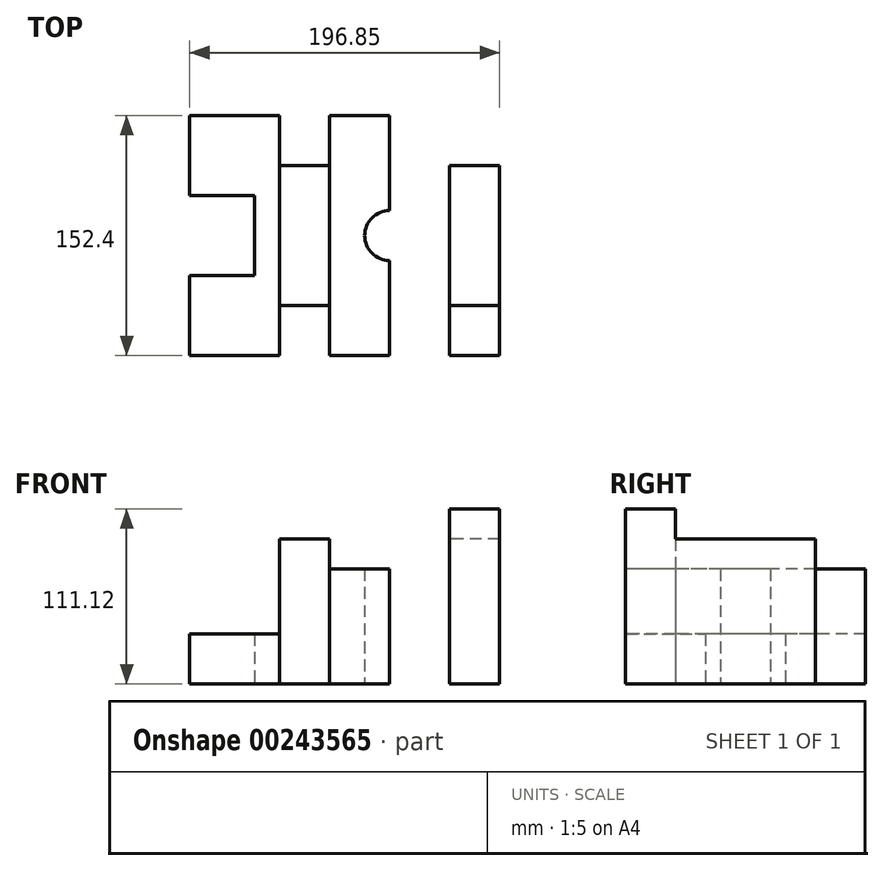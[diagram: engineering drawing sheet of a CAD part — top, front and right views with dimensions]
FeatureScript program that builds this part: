
annotation { "Feature Type Name" : "Feature", "Feature Type Description" : "" }
export const myFeature = defineFeature(function(context is Context, id is Id, definition is map)
    precondition{}
    {
        {
            var Q0;
            Q0=qCreatedBy(makeId("Top.planeOp"),FACE);
            var sketch = newSketch(context, id + "F0", { "sketchPlane" : qUnion([Q0])});
            skLineSegment(sketch, "E0.bottom", {"start": v(127, 76.2) * mm, "end": v(-127, 76.2) * mm});
            skLineSegment(sketch, "E0.top", {"start": v(127, -76.2) * mm, "end": v(-127, -76.2) * mm});
            skLineSegment(sketch, "E0.left", {"start": v(127, 76.2) * mm, "end": v(127, 25.4) * mm});
            skLineSegment(sketch, "E0.right", {"start": v(-127, 76.2) * mm, "end": v(-127, 25.4) * mm});
            skPoint(sketch, "E0.middle", {"position": v(0, 0) * mm});
            skCircle(sketch, "E1", {"center": v(0, 0) * mm, "radius": 15.88 * mm});
            skLineSegment(sketch, "E2.bottom", {"start": v(69.85, 76.2) * mm, "end": v(-69.85, 76.2) * mm});
            skLineSegment(sketch, "E2.top", {"start": v(69.85, -76.2) * mm, "end": v(-69.85, -76.2) * mm});
            skLineSegment(sketch, "E2.left", {"start": v(69.85, 76.2) * mm, "end": v(69.85, -76.2) * mm});
            skLineSegment(sketch, "E2.right", {"start": v(-69.85, 76.2) * mm, "end": v(-69.85, -76.2) * mm});
            skLineSegment(sketch, "E3.bottom", {"start": v(-69.85, 76.2) * mm, "end": v(-38.1, 76.2) * mm});
            skLineSegment(sketch, "E3.top", {"start": v(-69.85, -76.2) * mm, "end": v(-38.1, -76.2) * mm});
            skLineSegment(sketch, "E3.right", {"start": v(-38.1, 76.2) * mm, "end": v(-38.1, -76.2) * mm});
            skLineSegment(sketch, "E4", {"start": v(0, 76.2) * mm, "end": v(0, -76.2) * mm});
            skLineSegment(sketch, "E5.top", {"start": v(-69.85, 44.45) * mm, "end": v(-38.1, 44.45) * mm});
            skLineSegment(sketch, "E5.left", {"start": v(-69.85, 76.2) * mm, "end": v(-69.85, 44.45) * mm});
            skLineSegment(sketch, "E5.right", {"start": v(-38.1, 76.2) * mm, "end": v(-38.1, 44.45) * mm});
            skLineSegment(sketch, "E6.top", {"start": v(-69.85, -44.45) * mm, "end": v(-38.1, -44.45) * mm});
            skLineSegment(sketch, "E6.left", {"start": v(-69.85, -76.2) * mm, "end": v(-69.85, -44.45) * mm});
            skLineSegment(sketch, "E6.right", {"start": v(-38.1, -76.2) * mm, "end": v(-38.1, -44.45) * mm});
            skLineSegment(sketch, "E7.bottom", {"start": v(-127, 76.2) * mm, "end": v(-69.85, 76.2) * mm});
            skLineSegment(sketch, "E7.top", {"start": v(-127, 25.4) * mm, "end": v(-85.72, 25.4) * mm});
            skLineSegment(sketch, "E7.right", {"start": v(-69.85, 76.2) * mm, "end": v(-69.85, 25.4) * mm});
            skLineSegment(sketch, "E8.bottom", {"start": v(-127, -76.2) * mm, "end": v(-69.85, -76.2) * mm});
            skLineSegment(sketch, "E8.top", {"start": v(-127, -25.4) * mm, "end": v(-85.72, -25.4) * mm});
            skLineSegment(sketch, "E8.left", {"start": v(-127, -76.2) * mm, "end": v(-127, -25.4) * mm});
            skLineSegment(sketch, "E8.right", {"start": v(-69.85, -76.2) * mm, "end": v(-69.85, -25.4) * mm});
            skLineSegment(sketch, "E9.right", {"start": v(-85.72, 25.4) * mm, "end": v(-85.72, -25.4) * mm});
            skLineSegment(sketch, "E10.trimOffspring", {"start": v(-127, -25.4) * mm, "end": v(-127, -76.2) * mm});
            skLineSegment(sketch, "E11.MirrorCS", {"start": v(69.85, -76.2) * mm, "end": v(38.1, -76.2) * mm});
            skLineSegment(sketch, "E12.MirrorCS", {"start": v(127, -25.4) * mm, "end": v(85.72, -25.4) * mm});
            skLineSegment(sketch, "E13.MirrorCS", {"start": v(127, 25.4) * mm, "end": v(85.72, 25.4) * mm});
            skLineSegment(sketch, "E14.MirrorCS", {"start": v(69.85, -76.2) * mm, "end": v(69.85, -44.45) * mm});
            skLineSegment(sketch, "E15.MirrorCS", {"start": v(69.85, 76.2) * mm, "end": v(69.85, 44.45) * mm});
            skLineSegment(sketch, "E16.MirrorCS", {"start": v(127, -76.2) * mm, "end": v(127, -25.4) * mm});
            skLineSegment(sketch, "E17.MirrorCS", {"start": v(69.85, 76.2) * mm, "end": v(38.1, 76.2) * mm});
            skLineSegment(sketch, "E18.MirrorCS", {"start": v(127, 76.2) * mm, "end": v(69.85, 76.2) * mm});
            skLineSegment(sketch, "E19.MirrorCS", {"start": v(69.85, 76.2) * mm, "end": v(69.85, 25.4) * mm});
            skLineSegment(sketch, "E20.MirrorCS", {"start": v(127, -76.2) * mm, "end": v(69.85, -76.2) * mm});
            skLineSegment(sketch, "E21.MirrorCS", {"start": v(69.85, -44.45) * mm, "end": v(38.1, -44.45) * mm});
            skLineSegment(sketch, "E22.MirrorCS", {"start": v(85.72, 25.4) * mm, "end": v(85.72, -25.4) * mm});
            skLineSegment(sketch, "E23.MirrorCS", {"start": v(38.1, -76.2) * mm, "end": v(38.1, -44.45) * mm});
            skLineSegment(sketch, "E24.MirrorCS", {"start": v(127, -25.4) * mm, "end": v(127, -76.2) * mm});
            skLineSegment(sketch, "E25.MirrorCS", {"start": v(69.85, -76.2) * mm, "end": v(69.85, -25.4) * mm});
            skLineSegment(sketch, "E26.MirrorCS", {"start": v(38.1, 76.2) * mm, "end": v(38.1, -76.2) * mm});
            skLineSegment(sketch, "E27.MirrorCS", {"start": v(38.1, 76.2) * mm, "end": v(38.1, 44.45) * mm});
            skLineSegment(sketch, "E28.MirrorCS", {"start": v(69.85, 44.45) * mm, "end": v(38.1, 44.45) * mm});
            skSolve(sketch);
        }
        {
            var Q0;
            {var subQ1=sQuery(id+"F0.wireOp",EDGE,"E2.right");Q0=makeQuery(id+"F0.imprint","IMPRINT",FACE,{"disambiguationData":[TD([[makeQuery(id+"F0.imprint","IMPRINT",EDGE,{"derivedFrom":subQ1}),-1.0]])]});}
            var Q1;
            {var subQ7=sQuery(id+"F0.wireOp",EDGE,"E18.MirrorCS");Q1=makeQuery(id+"F0.imprint","IMPRINT",FACE,{"disambiguationData":[TD([[makeQuery(id+"F0.imprint","IMPRINT",EDGE,{"derivedFrom":subQ7}),1.0]])]});}
            var Q2;
            {var subQ2=sQuery(id+"F0.wireOp",EDGE,"E2.right");Q2=makeQuery(id+"F0.imprint","IMPRINT",FACE,{"disambiguationData":[TD([[makeQuery(id+"F0.imprint","IMPRINT",EDGE,{"derivedFrom":subQ2}),1.0]])]});}
            var Q3;
            {var subQ0=sQuery(id+"F0.wireOp",EDGE,"E3.bottom");Q3=makeQuery(id+"F0.imprint","IMPRINT",FACE,{"disambiguationData":[TD([[makeQuery(id+"F0.imprint","IMPRINT",EDGE,{"derivedFrom":subQ0}),-1.0]])]});}
            var Q4;
            {var subQ0=sQuery(id+"F0.wireOp",EDGE,"E3.top");Q4=makeQuery(id+"F0.imprint","IMPRINT",FACE,{"disambiguationData":[TD([[makeQuery(id+"F0.imprint","IMPRINT",EDGE,{"derivedFrom":subQ0}),1.0]])]});}
            var Q5;
            Q5=makeQuery(id+"F0.imprint","IMPRINT",FACE,{"disambiguationData":[TD([[makeQuery(id+"F0.imprint","IMPRINT",EDGE,{"derivedFrom":sQuery(id+"F0.wireOp",EDGE,"E3.right")}),1.0]])]});
            var Q6;
            {var subQ11=sQuery(id+"F0.wireOp",EDGE,"E27.MirrorCS");Q6=makeQuery(id+"F0.imprint","IMPRINT",FACE,{"disambiguationData":[TD([[makeQuery(id+"F0.imprint","IMPRINT",EDGE,{"derivedFrom":subQ11}),-1.0]])]});}
            var Q7;
            {var subQ0=sQuery(id+"F0.wireOp",EDGE,"E21.MirrorCS");Q7=makeQuery(id+"F0.imprint","IMPRINT",FACE,{"disambiguationData":[TD([[makeQuery(id+"F0.imprint","IMPRINT",EDGE,{"derivedFrom":subQ0}),1.0]])]});}
            var Q8;
            {var subQ1=sQuery(id+"F0.wireOp",EDGE,"E21.MirrorCS");Q8=makeQuery(id+"F0.imprint","IMPRINT",FACE,{"disambiguationData":[TD([[makeQuery(id+"F0.imprint","IMPRINT",EDGE,{"derivedFrom":subQ1}),-1.0]])]});}
            var Q9;
            {var subQ0=sQuery(id+"F0.wireOp",EDGE,"E17.MirrorCS");Q9=makeQuery(id+"F0.imprint","IMPRINT",FACE,{"disambiguationData":[TD([[makeQuery(id+"F0.imprint","IMPRINT",EDGE,{"derivedFrom":subQ0}),1.0]])]});}
            extrude(context, id + "F1", {"entities" : qUnion([Q0, Q1, Q2, Q3, Q4, Q5, Q6, Q7, Q8, Q9]), "depth" : 31.75 * mm});
        }
        {
            var Q0;
            Q0=makeQuery(id+"F1.opExtrude","CAP_FACE",FACE,{"disambiguationData":[OSD([sQuery(id+"F0.wireOp",EDGE,"E1"),sQuery(id+"F0.wireOp",EDGE,"E2.bottom"),sQuery(id+"F0.wireOp",EDGE,"E2.top"),sQuery(id+"F0.wireOp",EDGE,"E3.bottom"),sQuery(id+"F0.wireOp",EDGE,"E3.top"),sQuery(id+"F0.wireOp",EDGE,"E7.bottom"),sQuery(id+"F0.wireOp",EDGE,"E0.right"),sQuery(id+"F0.wireOp",EDGE,"E8.bottom"),sQuery(id+"F0.wireOp",EDGE,"E7.top"),sQuery(id+"F0.wireOp",EDGE,"E8.top"),sQuery(id+"F0.wireOp",EDGE,"E9.right"),sQuery(id+"F0.wireOp",EDGE,"E10.trimOffspring"),sQuery(id+"F0.wireOp",EDGE,"E18.MirrorCS"),sQuery(id+"F0.wireOp",EDGE,"E12.MirrorCS"),sQuery(id+"F0.wireOp",EDGE,"E20.MirrorCS"),sQuery(id+"F0.wireOp",EDGE,"E22.MirrorCS"),sQuery(id+"F0.wireOp",EDGE,"E17.MirrorCS"),sQuery(id+"F0.wireOp",EDGE,"E11.MirrorCS"),sQuery(id+"F0.wireOp",EDGE,"E13.MirrorCS"),sQuery(id+"F0.wireOp",EDGE,"E0.left"),sQuery(id+"F0.wireOp",EDGE,"E24.MirrorCS")])],"isStart":false});
            var sketch = newSketch(context, id + "F2", { "sketchPlane" : qUnion([Q0])});
            skLineSegment(sketch, "E29.bottom", {"start": v(127, 76.2) * mm, "end": v(-127, 76.2) * mm});
            skLineSegment(sketch, "E29.top", {"start": v(127, -76.2) * mm, "end": v(-127, -76.2) * mm});
            skLineSegment(sketch, "E29.left", {"start": v(127, 76.2) * mm, "end": v(127, 25.4) * mm});
            skLineSegment(sketch, "E29.right", {"start": v(-127, 76.2) * mm, "end": v(-127, 25.4) * mm});
            skPoint(sketch, "E29.middle", {"position": v(0, 0) * mm});
            skCircle(sketch, "E30", {"center": v(0, 0) * mm, "radius": 15.88 * mm});
            skLineSegment(sketch, "E31.bottom", {"start": v(69.85, 76.2) * mm, "end": v(-69.85, 76.2) * mm});
            skLineSegment(sketch, "E31.top", {"start": v(69.85, -76.2) * mm, "end": v(-69.85, -76.2) * mm});
            skLineSegment(sketch, "E31.left", {"start": v(69.85, 76.2) * mm, "end": v(69.85, -76.2) * mm});
            skLineSegment(sketch, "E31.right", {"start": v(-69.85, 76.2) * mm, "end": v(-69.85, -76.2) * mm});
            skLineSegment(sketch, "E32.bottom", {"start": v(-69.85, 76.2) * mm, "end": v(-38.1, 76.2) * mm});
            skLineSegment(sketch, "E32.top", {"start": v(-69.85, -76.2) * mm, "end": v(-38.1, -76.2) * mm});
            skLineSegment(sketch, "E32.right", {"start": v(-38.1, 76.2) * mm, "end": v(-38.1, -76.2) * mm});
            skLineSegment(sketch, "E33", {"start": v(0, 76.2) * mm, "end": v(0, -76.2) * mm});
            skLineSegment(sketch, "E34.top", {"start": v(-69.85, 44.45) * mm, "end": v(-38.1, 44.45) * mm});
            skLineSegment(sketch, "E34.left", {"start": v(-69.85, 76.2) * mm, "end": v(-69.85, 44.45) * mm});
            skLineSegment(sketch, "E34.right", {"start": v(-38.1, 76.2) * mm, "end": v(-38.1, 44.45) * mm});
            skLineSegment(sketch, "E35.top", {"start": v(-69.85, -44.45) * mm, "end": v(-38.1, -44.45) * mm});
            skLineSegment(sketch, "E35.left", {"start": v(-69.85, -76.2) * mm, "end": v(-69.85, -44.45) * mm});
            skLineSegment(sketch, "E35.right", {"start": v(-38.1, -76.2) * mm, "end": v(-38.1, -44.45) * mm});
            skLineSegment(sketch, "E36.bottom", {"start": v(-127, 76.2) * mm, "end": v(-69.85, 76.2) * mm});
            skLineSegment(sketch, "E36.top", {"start": v(-127, 25.4) * mm, "end": v(-85.72, 25.4) * mm});
            skLineSegment(sketch, "E36.right", {"start": v(-69.85, 76.2) * mm, "end": v(-69.85, 25.4) * mm});
            skLineSegment(sketch, "E37.bottom", {"start": v(-127, -76.2) * mm, "end": v(-69.85, -76.2) * mm});
            skLineSegment(sketch, "E37.top", {"start": v(-127, -25.4) * mm, "end": v(-85.72, -25.4) * mm});
            skLineSegment(sketch, "E37.left", {"start": v(-127, -76.2) * mm, "end": v(-127, -25.4) * mm});
            skLineSegment(sketch, "E37.right", {"start": v(-69.85, -76.2) * mm, "end": v(-69.85, -25.4) * mm});
            skLineSegment(sketch, "E38.right", {"start": v(-85.72, 25.4) * mm, "end": v(-85.72, -25.4) * mm});
            skLineSegment(sketch, "E39.trimOffspring", {"start": v(-127, -25.4) * mm, "end": v(-127, -76.2) * mm});
            skLineSegment(sketch, "E40.MirrorCS", {"start": v(69.85, -76.2) * mm, "end": v(38.1, -76.2) * mm});
            skLineSegment(sketch, "E41.MirrorCS", {"start": v(127, -25.4) * mm, "end": v(85.72, -25.4) * mm});
            skLineSegment(sketch, "E42.MirrorCS", {"start": v(127, 25.4) * mm, "end": v(85.72, 25.4) * mm});
            skLineSegment(sketch, "E43.MirrorCS", {"start": v(69.85, -76.2) * mm, "end": v(69.85, -44.45) * mm});
            skLineSegment(sketch, "E44.MirrorCS", {"start": v(69.85, 76.2) * mm, "end": v(69.85, 44.45) * mm});
            skLineSegment(sketch, "E45.MirrorCS", {"start": v(127, -76.2) * mm, "end": v(127, -25.4) * mm});
            skLineSegment(sketch, "E46.MirrorCS", {"start": v(69.85, 76.2) * mm, "end": v(38.1, 76.2) * mm});
            skLineSegment(sketch, "E47.MirrorCS", {"start": v(127, 76.2) * mm, "end": v(69.85, 76.2) * mm});
            skLineSegment(sketch, "E48.MirrorCS", {"start": v(69.85, 76.2) * mm, "end": v(69.85, 25.4) * mm});
            skLineSegment(sketch, "E49.MirrorCS", {"start": v(127, -76.2) * mm, "end": v(69.85, -76.2) * mm});
            skLineSegment(sketch, "E50.MirrorCS", {"start": v(69.85, -44.45) * mm, "end": v(38.1, -44.45) * mm});
            skLineSegment(sketch, "E51.MirrorCS", {"start": v(85.72, 25.4) * mm, "end": v(85.72, -25.4) * mm});
            skLineSegment(sketch, "E52.MirrorCS", {"start": v(38.1, -76.2) * mm, "end": v(38.1, -44.45) * mm});
            skLineSegment(sketch, "E53.MirrorCS", {"start": v(127, -25.4) * mm, "end": v(127, -76.2) * mm});
            skLineSegment(sketch, "E54.MirrorCS", {"start": v(69.85, -76.2) * mm, "end": v(69.85, -25.4) * mm});
            skLineSegment(sketch, "E55.MirrorCS", {"start": v(38.1, 76.2) * mm, "end": v(38.1, -76.2) * mm});
            skLineSegment(sketch, "E56.MirrorCS", {"start": v(38.1, 76.2) * mm, "end": v(38.1, 44.45) * mm});
            skLineSegment(sketch, "E57.MirrorCS", {"start": v(69.85, 44.45) * mm, "end": v(38.1, 44.45) * mm});
            skSolve(sketch);
        }
        {
            var Q0;
            {var subQ0=sQuery(id+"F2.wireOp",EDGE,"E32.top");Q0=makeQuery(id+"F2.imprint","IMPRINT",FACE,{"disambiguationData":[TD([[makeQuery(id+"F2.imprint","IMPRINT",EDGE,{"derivedFrom":subQ0}),1.0]])]});}
            var Q1;
            {var subQ0=sQuery(id+"F2.wireOp",EDGE,"E50.MirrorCS");Q1=makeQuery(id+"F2.imprint","IMPRINT",FACE,{"disambiguationData":[TD([[makeQuery(id+"F2.imprint","IMPRINT",EDGE,{"derivedFrom":subQ0}),1.0]])]});}
            var Q2;
            {var subQ0=sQuery(id+"F2.wireOp",EDGE,"E46.MirrorCS");Q2=makeQuery(id+"F2.imprint","IMPRINT",FACE,{"disambiguationData":[TD([[makeQuery(id+"F2.imprint","IMPRINT",EDGE,{"derivedFrom":subQ0}),-1.0]])]});}
            var Q3;
            {var subQ0=sQuery(id+"F2.wireOp",EDGE,"E32.bottom");Q3=makeQuery(id+"F2.imprint","IMPRINT",FACE,{"disambiguationData":[TD([[makeQuery(id+"F2.imprint","IMPRINT",EDGE,{"derivedFrom":subQ0}),-1.0]])]});}
            extrude(context, id + "F3", {"entities" : qUnion([Q0, Q1, Q2, Q3]), "operationType" : NewBodyOperationType.ADD, "depth" : 79.38 * mm});
        }
        {
            var Q0;
            {var subQ3=sQuery(id+"F2.wireOp",EDGE,"E31.right");Q0=makeQuery(id+"F2.imprint","IMPRINT",FACE,{"disambiguationData":[TD([[makeQuery(id+"F2.imprint","IMPRINT",EDGE,{"derivedFrom":subQ3}),1.0]])]});}
            var Q1;
            {var subQ1=sQuery(id+"F2.wireOp",EDGE,"E50.MirrorCS");Q1=makeQuery(id+"F2.imprint","IMPRINT",FACE,{"disambiguationData":[TD([[makeQuery(id+"F2.imprint","IMPRINT",EDGE,{"derivedFrom":subQ1}),-1.0]])]});}
            extrude(context, id + "F4", {"entities" : qUnion([Q0, Q1]), "operationType" : NewBodyOperationType.ADD, "depth" : 60.32 * mm});
        }
        {
            var Q0;
            {var subQ0=sQuery(id+"F0.wireOp",EDGE,"E11.MirrorCS");var subQ1=sQuery(id+"F0.wireOp",EDGE,"E20.MirrorCS");var subQ2=sQuery(id+"F0.wireOp",EDGE,"E8.bottom");var subQ3=sQuery(id+"F0.wireOp",EDGE,"E3.top");var subQ4=sQuery(id+"F0.wireOp",EDGE,"E2.top");var subQ5=sQuery(id+"F0.wireOp",EDGE,"E1");var subQ6=sQuery(id+"F0.wireOp",EDGE,"E17.MirrorCS");var subQ7=sQuery(id+"F0.wireOp",EDGE,"E18.MirrorCS");var subQ8=sQuery(id+"F0.wireOp",EDGE,"E7.bottom");var subQ9=sQuery(id+"F0.wireOp",EDGE,"E3.bottom");var subQ10=sQuery(id+"F0.wireOp",EDGE,"E2.bottom");Q0=makeQuery(id+"F4.boolean.opBoolean","SPLIT",FACE,{"disambiguationData":[TD([makeQuery(id+"F1.opExtrude","SWEPT_FACE",FACE,{"disambiguationData":[OSD([subQ5])]})])],"derivedFrom":makeQuery(id+"F1.opExtrude","CAP_FACE",FACE,{"disambiguationData":[OSD([subQ5,subQ10,subQ4,subQ9,subQ3,subQ8,sQuery(id+"F0.wireOp",EDGE,"E0.right"),subQ2,sQuery(id+"F0.wireOp",EDGE,"E7.top"),sQuery(id+"F0.wireOp",EDGE,"E8.top"),sQuery(id+"F0.wireOp",EDGE,"E9.right"),sQuery(id+"F0.wireOp",EDGE,"E10.trimOffspring"),subQ7,sQuery(id+"F0.wireOp",EDGE,"E12.MirrorCS"),subQ1,sQuery(id+"F0.wireOp",EDGE,"E22.MirrorCS"),subQ6,subQ0,sQuery(id+"F0.wireOp",EDGE,"E13.MirrorCS"),sQuery(id+"F0.wireOp",EDGE,"E0.left"),sQuery(id+"F0.wireOp",EDGE,"E24.MirrorCS")])],"isStart":false})});}
            extrude(context, id + "F5", {"entities" : qUnion([Q0]), "operationType" : NewBodyOperationType.ADD, "depth" : 41.27 * mm});
        }
    });
